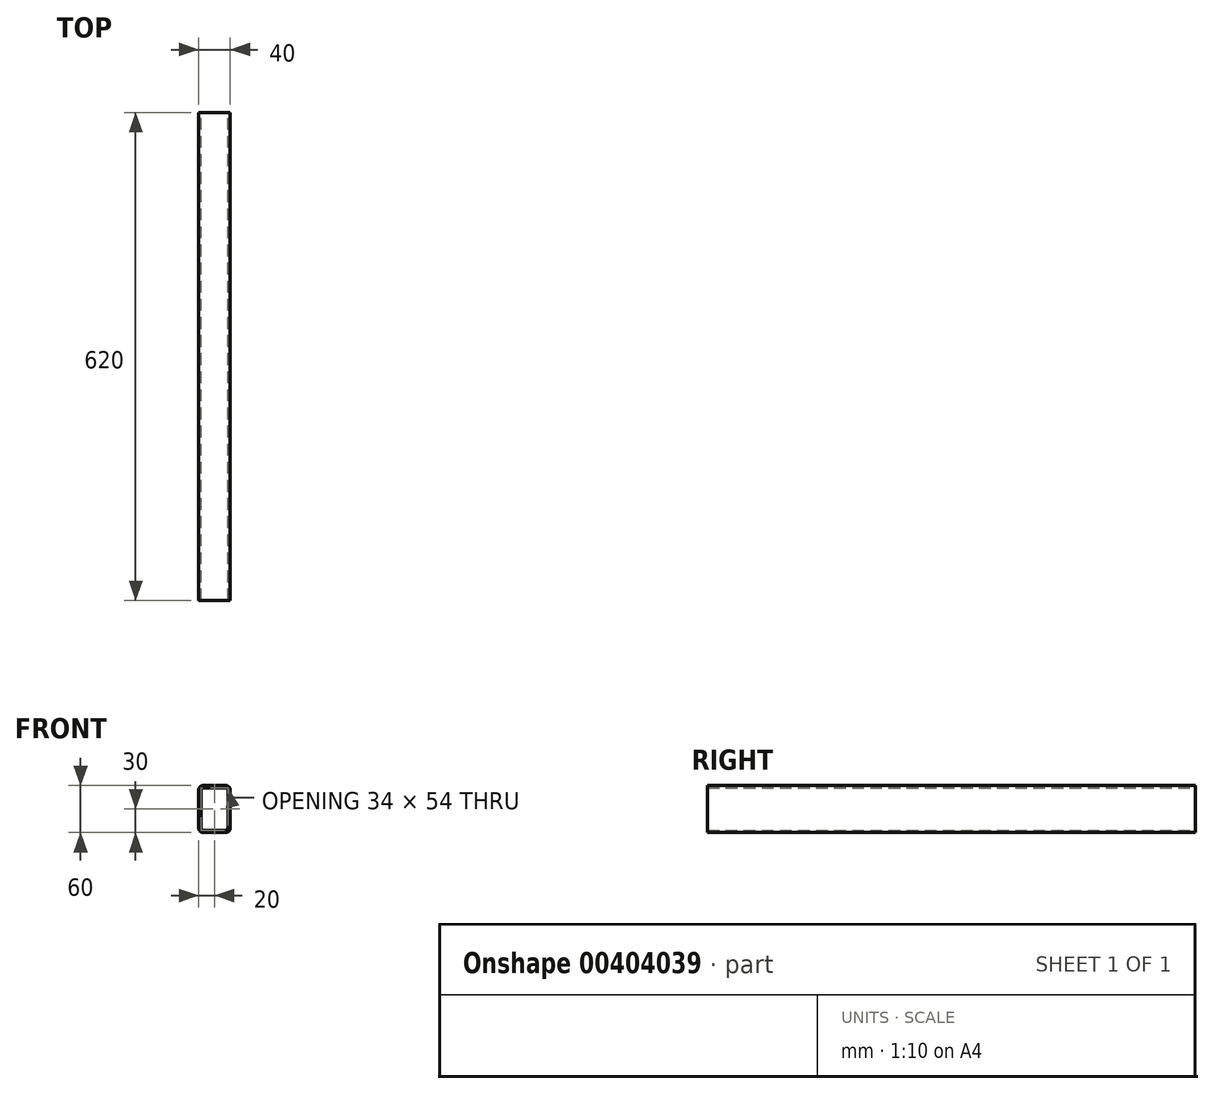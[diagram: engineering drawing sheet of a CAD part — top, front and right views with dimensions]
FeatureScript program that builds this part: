
annotation { "Feature Type Name" : "Feature", "Feature Type Description" : "" }
export const myFeature = defineFeature(function(context is Context, id is Id, definition is map)
    precondition{}
    {
        {
            var Q0;
            Q0=qCreatedBy(makeId("Front.planeOp"),FACE);
            var sketch = newSketch(context, id + "F0", { "sketchPlane" : qUnion([Q0])});
            skLineSegment(sketch, "E0.bottom", {"start": v(-14, 30) * mm, "end": v(14, 30) * mm});
            skLineSegment(sketch, "E0.top", {"start": v(-14, -30) * mm, "end": v(14, -30) * mm});
            skLineSegment(sketch, "E0.left", {"start": v(-20, 24) * mm, "end": v(-20, -24) * mm});
            skLineSegment(sketch, "E0.right", {"start": v(20, 24) * mm, "end": v(20, -24) * mm});
            skPoint(sketch, "E1.visualSharp", {"position": v(-20, 30) * mm});
            skArc(sketch, "E1.filletArc", {"start": v(-14, 30) * mm, "mid": v(-18.24, 28.24) * mm, "end": v(-20, 24) * mm});
            skPoint(sketch, "E2.visualSharp", {"position": v(-20, -30) * mm});
            skArc(sketch, "E2.filletArc", {"start": v(-20, -24) * mm, "mid": v(-18.24, -28.24) * mm, "end": v(-14, -30) * mm});
            skPoint(sketch, "E3.visualSharp", {"position": v(20, -30) * mm});
            skArc(sketch, "E3.filletArc", {"start": v(14, -30) * mm, "mid": v(18.24, -28.24) * mm, "end": v(20, -24) * mm});
            skPoint(sketch, "E4.visualSharp", {"position": v(20, 30) * mm});
            skArc(sketch, "E4.filletArc", {"start": v(20, 24) * mm, "mid": v(18.24, 28.24) * mm, "end": v(14, 30) * mm});
            skLineSegment(sketch, "E5.0", {"start": v(-17, 24) * mm, "end": v(-17, -24) * mm});
            skLineSegment(sketch, "E6.0", {"start": v(-14, 27) * mm, "end": v(14, 27) * mm});
            skArc(sketch, "E6.1", {"start": v(17, 24) * mm, "mid": v(16.12, 26.12) * mm, "end": v(14, 27) * mm});
            skLineSegment(sketch, "E6.2", {"start": v(17, 24) * mm, "end": v(17, -24) * mm});
            skArc(sketch, "E6.4", {"start": v(-17, -24) * mm, "mid": v(-16.12, -26.12) * mm, "end": v(-14, -27) * mm});
            skLineSegment(sketch, "E6.5", {"start": v(-14, -27) * mm, "end": v(14, -27) * mm});
            skArc(sketch, "E6.6", {"start": v(14, -27) * mm, "mid": v(16.12, -26.12) * mm, "end": v(17, -24) * mm});
            skArc(sketch, "E7.0", {"start": v(-14, 27) * mm, "mid": v(-16.12, 26.12) * mm, "end": v(-17, 24) * mm});
            skSolve(sketch);
        }
        {
            var Q0;
            Q0=makeQuery(id+"F0.imprint","IMPRINT",FACE,{"disambiguationData":[TD([[makeQuery(id+"F0.imprint","IMPRINT",EDGE,{"derivedFrom":sQuery(id+"F0.wireOp",EDGE,"E0.bottom")}),-1.0]])]});
            extrude(context, id + "F1", {"entities" : qUnion([Q0]), "depth" : 620 * mm});
        }
    });
